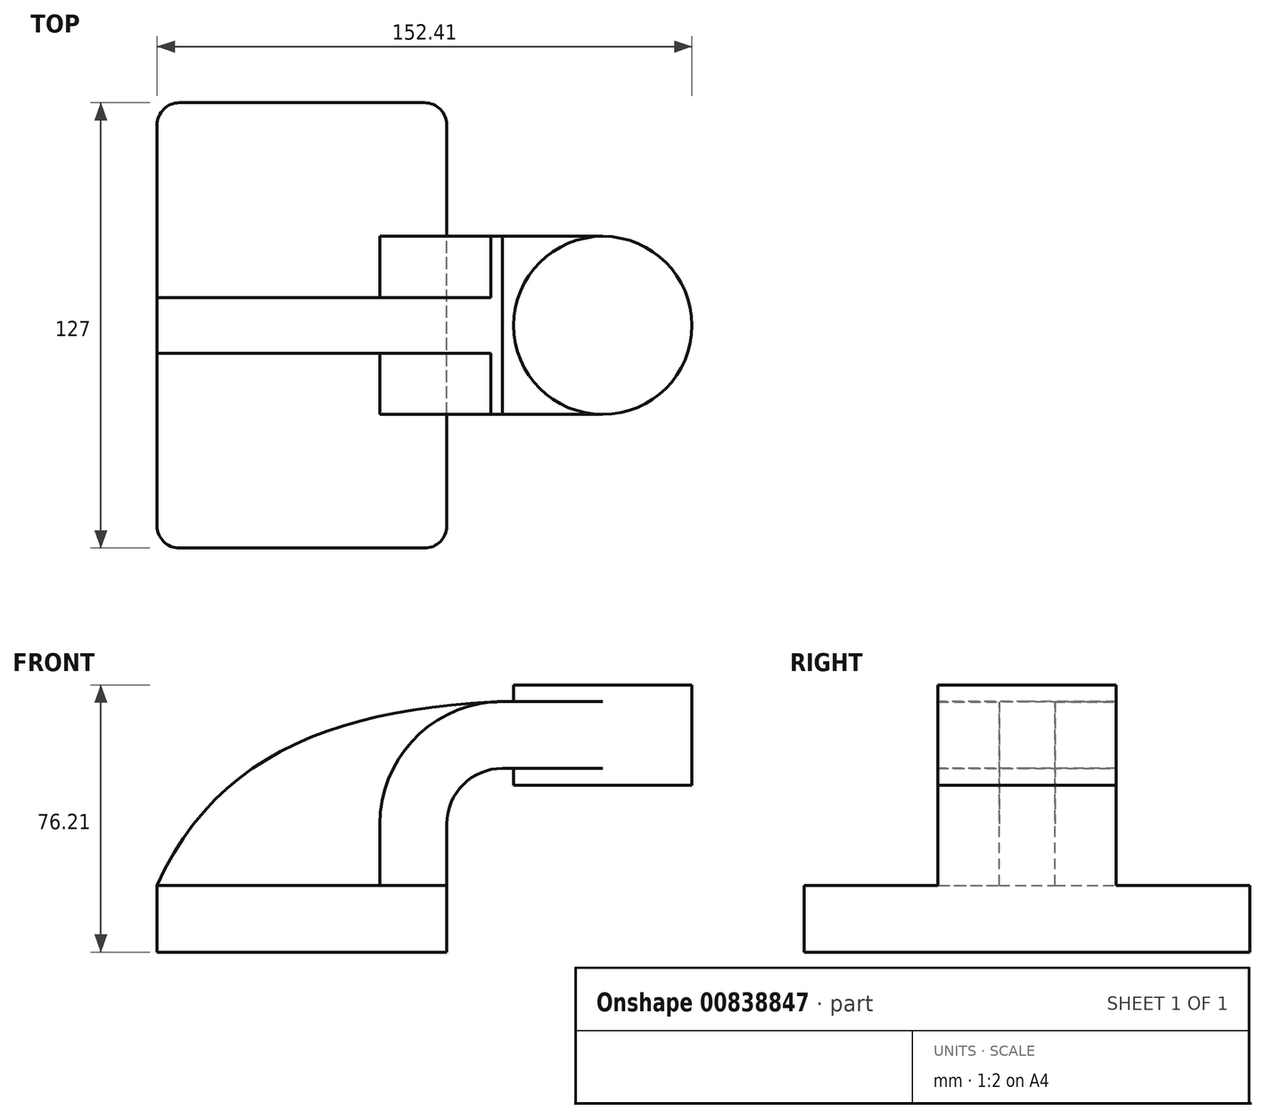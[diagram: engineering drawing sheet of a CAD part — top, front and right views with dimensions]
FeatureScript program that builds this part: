
annotation { "Feature Type Name" : "Feature", "Feature Type Description" : "" }
export const myFeature = defineFeature(function(context is Context, id is Id, definition is map)
    precondition{}
    {
        {
            var Q0;
            Q0=qCreatedBy(makeId("Front.planeOp"),FACE);
            var sketch = newSketch(context, id + "F0", { "sketchPlane" : qUnion([Q0])});
            skLineSegment(sketch, "E0.bottom", {"start": v(-41.28, -9.52) * mm, "end": v(41.28, -9.52) * mm});
            skLineSegment(sketch, "E0.top", {"start": v(-41.28, 9.53) * mm, "end": v(41.28, 9.53) * mm});
            skLineSegment(sketch, "E0.left", {"start": v(-41.28, -9.52) * mm, "end": v(-41.28, 9.53) * mm});
            skLineSegment(sketch, "E0.right", {"start": v(41.28, -9.52) * mm, "end": v(41.28, 9.53) * mm});
            skPoint(sketch, "E0.middle", {"position": v(0, 0) * mm});
            skLineSegment(sketch, "E1", {"start": v(41.28, 9.53) * mm, "end": v(41.28, 27) * mm});
            skLineSegment(sketch, "E2.bottom", {"start": v(111.12, 38.1) * mm, "end": v(60.32, 38.1) * mm});
            skLineSegment(sketch, "E2.top", {"start": v(111.12, 66.68) * mm, "end": v(60.32, 66.68) * mm});
            skLineSegment(sketch, "E2.left", {"start": v(111.12, 38.1) * mm, "end": v(111.12, 66.68) * mm});
            skLineSegment(sketch, "E2.right", {"start": v(60.33, 38.1) * mm, "end": v(60.33, 66.68) * mm});
            skPoint(sketch, "E2.middle", {"position": v(85.72, 52.39) * mm});
            skPoint(sketch, "E3.startSnap0", {"position": v(111.12, 52.39) * mm});
            skPoint(sketch, "E4.orphan", {"position": v(51.2, 52.39) * mm});
            skArc(sketch, "E5", {"start": v(41.27, 27) * mm, "mid": v(45.92, 38.23) * mm, "end": v(57.15, 42.88) * mm});
            skLineSegment(sketch, "E6", {"start": v(57.15, 42.88) * mm, "end": v(85.72, 42.88) * mm});
            skLineSegment(sketch, "E7.0", {"start": v(57.15, 61.93) * mm, "end": v(85.72, 61.93) * mm});
            skArc(sketch, "E7.1", {"start": v(22.22, 27) * mm, "mid": v(32.45, 51.7) * mm, "end": v(57.15, 61.93) * mm});
            skLineSegment(sketch, "E7.2", {"start": v(22.22, 9.53) * mm, "end": v(22.22, 27) * mm});
            skLineSegment(sketch, "E8", {"start": v(85.72, 38.1) * mm, "end": v(85.72, 66.68) * mm});
            skFitSpline(sketch, "E9", {"points": [v(-41.28, 9.53) * mm, v(57.15, 61.93) * mm], "startDerivative": vector(51.53, 114.57) * mm, "endDerivative": vector(137.75, 5.7) * mm});
            skSolve(sketch);
        }
        {
            var Q0;
            Q0=makeQuery(id+"F0.imprint","IMPRINT",FACE,{"disambiguationData":[TD([[makeQuery(id+"F0.imprint","IMPRINT",EDGE,{"derivedFrom":sQuery(id+"F0.wireOp",EDGE,"E0.bottom")}),1.0]])]});
            extrude(context, id + "F1", {"entities" : qUnion([Q0]), "endBound" : BoundingType.SYMMETRIC, "depth" : 127 * mm, "offsetDistance" : 25.4 * mm});
        }
        {
            var Q0;
            {var subQ1=sQuery(id+"F0.wireOp",EDGE,"E1");Q0=makeQuery(id+"F0.imprint","IMPRINT",FACE,{"disambiguationData":[TD([[makeQuery(id+"F0.imprint","IMPRINT",EDGE,{"derivedFrom":subQ1}),1.0]])]});}
            var Q1;
            {var subQ0=sQuery(id+"F0.wireOp",EDGE,"E6");var subQ1=sQuery(id+"F0.wireOp",EDGE,"E2.right");var subQ2=makeQuery(id+"F0.imprint","INTERSECT",VERTEX,{"derivedFrom":[subQ1,subQ0]});Q1=makeQuery(id+"F0.imprint","IMPRINT",FACE,{"disambiguationData":[TD([[makeQuery(id+"F0.imprint","IMPRINT",EDGE,{"disambiguationData":[TD([[subQ2,-1.0]])],"derivedFrom":subQ1}),-1.0]])]});}
            extrude(context, id + "F2", {"entities" : qUnion([Q0, Q1]), "operationType" : NewBodyOperationType.ADD, "endBound" : BoundingType.SYMMETRIC, "depth" : 50.8 * mm, "offsetDistance" : 25.4 * mm});
        }
        {
            var Q0;
            {var subQ3=sQuery(id+"F0.wireOp",EDGE,"E7.2");Q0=makeQuery(id+"F0.imprint","IMPRINT",FACE,{"disambiguationData":[TD([[makeQuery(id+"F0.imprint","IMPRINT",EDGE,{"derivedFrom":subQ3}),1.0]])]});}
            extrude(context, id + "F3", {"entities" : qUnion([Q0]), "operationType" : NewBodyOperationType.ADD, "endBound" : BoundingType.SYMMETRIC, "depth" : 15.88 * mm, "offsetDistance" : 25.4 * mm});
        }
        {
            var Q0;
            {var subQ4=sQuery(id+"F0.wireOp",EDGE,"E2.left");Q0=makeQuery(id+"F0.imprint","IMPRINT",FACE,{"disambiguationData":[TD([[makeQuery(id+"F0.imprint","IMPRINT",EDGE,{"derivedFrom":subQ4}),1.0]])]});}
            var Q1;
            Q1=sQuery(id+"F0.wireOp",EDGE,"E8");
            revolve(context, id + "F4", {"operationType" : NewBodyOperationType.ADD, "surfaceOperationType" : NewSurfaceOperationType.NEW, "entities" : qUnion([Q0]), "axis" : qUnion([Q1]), "revolveType" : RevolveType.FULL});
        }
        {
            var Q0;
            Q0=makeQuery(id+"F1.opExtrude","CAP_EDGE",EDGE,{"disambiguationData":[OSD([sQuery(id+"F0.wireOp",EDGE,"E0.left")])],"isStart":false});
            var Q1;
            Q1=makeQuery(id+"F1.opExtrude","CAP_EDGE",EDGE,{"disambiguationData":[OSD([sQuery(id+"F0.wireOp",EDGE,"E0.right")])],"isStart":false});
            var Q2;
            Q2=makeQuery(id+"F1.opExtrude","CAP_EDGE",EDGE,{"disambiguationData":[OSD([sQuery(id+"F0.wireOp",EDGE,"E0.right")])],"isStart":true});
            var Q3;
            Q3=makeQuery(id+"F1.opExtrude","CAP_EDGE",EDGE,{"disambiguationData":[OSD([sQuery(id+"F0.wireOp",EDGE,"E0.left")])],"isStart":true});
            fillet(context, id + "F5", {"entities" : qUnion([Q0, Q1, Q2, Q3]), "radius" : 6.35 * mm, "tangentPropagation" : true, "allowEdgeOverflow" : false});
        }
    });
